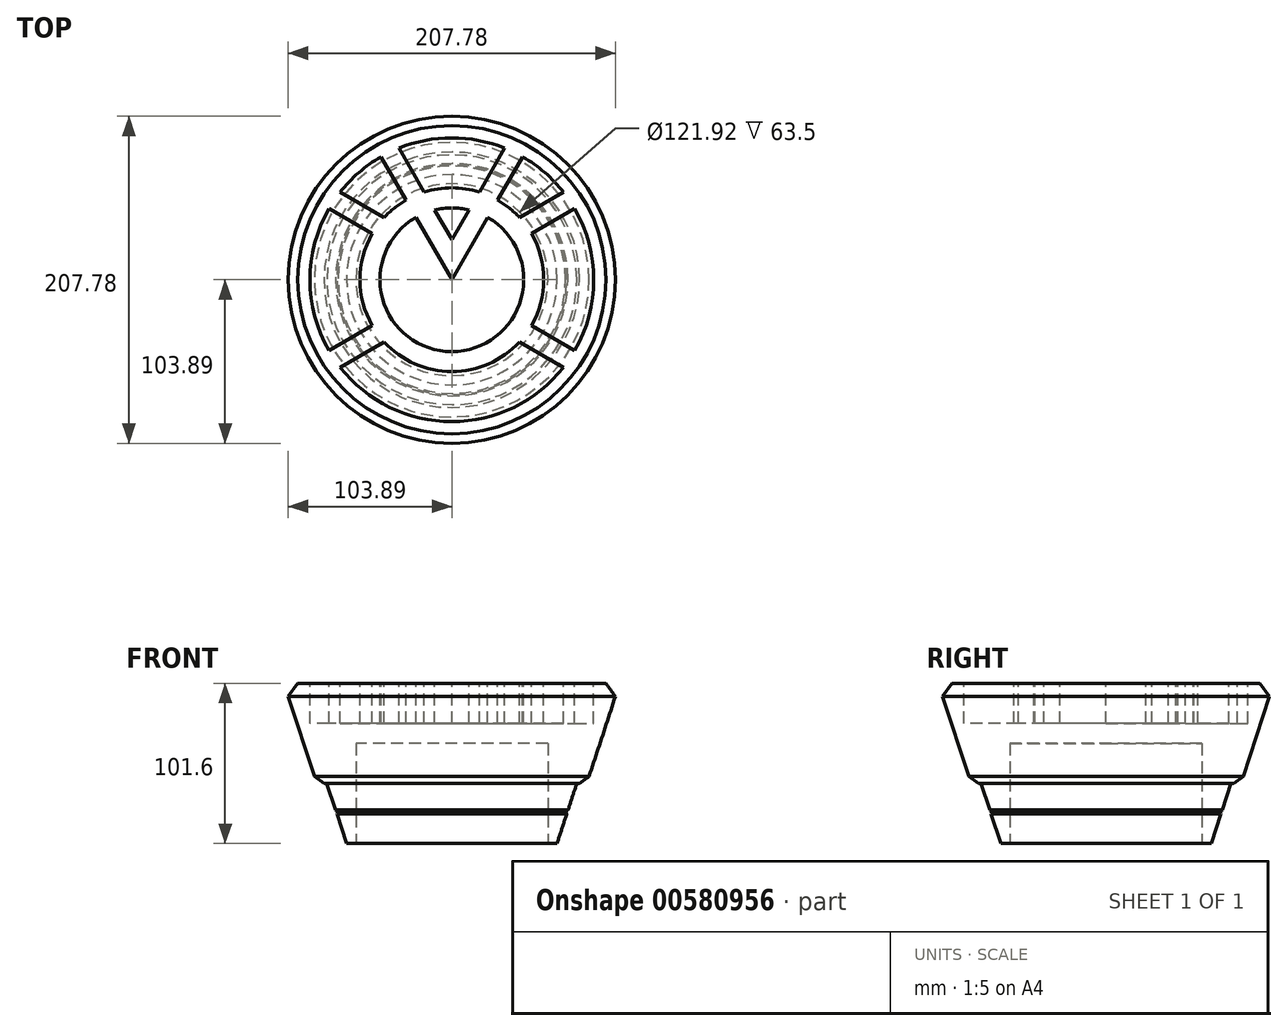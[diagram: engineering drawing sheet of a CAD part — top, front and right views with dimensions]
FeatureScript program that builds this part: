
annotation { "Feature Type Name" : "Feature", "Feature Type Description" : "" }
export const myFeature = defineFeature(function(context is Context, id is Id, definition is map)
    precondition{}
    {
        {
            var Q0;
            Q0=qCreatedBy(makeId("Top.planeOp"),FACE);
            var sketch = newSketch(context, id + "F0", { "sketchPlane" : qUnion([Q0])});
            skCircle(sketch, "E0", {"center": v(0, 0) * mm, "radius": 66.85 * mm});
            skSolve(sketch);
        }
        {
            var Q0;
            Q0=qCreatedBy(makeId("Top.planeOp"),FACE);
            cPlane(context, id + "F1", {"entities" : qUnion([Q0]), "cplaneType" : CPlaneType.OFFSET, "offset" : 101.6 * mm, "width" : 152.4 * mm, "height" : 152.4 * mm});
        }
        {
            var Q0;
            Q0=qCreatedBy(id+"F1.planeOp",FACE);
            var sketch = newSketch(context, id + "F2", { "sketchPlane" : qUnion([Q0])});
            skCircle(sketch, "E1", {"center": v(0, 0) * mm, "radius": 100.28 * mm});
            skSolve(sketch);
        }
        {
            var Q0;
            Q0=makeQuery(id+"F2.imprint","IMPRINT",FACE,{"disambiguationData":[TD([[makeQuery(id+"F2.imprint","IMPRINT",EDGE,{"derivedFrom":sQuery(id+"F2.wireOp",EDGE,"E1")}),1.0]])]});
            var Q1;
            Q1=makeQuery(id+"F0.imprint","IMPRINT",FACE,{"disambiguationData":[TD([[makeQuery(id+"F0.imprint","IMPRINT",EDGE,{"derivedFrom":sQuery(id+"F0.wireOp",EDGE,"E0")}),1.0]])]});
            var Q2;
            Q2=sQuery(id+"F2.wireOp",EDGE,"Eyu8YDiN-lEGU-Wuxt-0ncA-RZLAWeJK4OgB");
            var Q3;
            Q3=sQuery(id+"F0.wireOp",EDGE,"fgfE4CqQ-t5n6-ucAx-yhIW-5wF2yx0Jya2k");
            loft(context, id + "F3", {"sheetProfilesArray" : [{ "sheetProfileEntities" : qUnion([Q0]) }, { "sheetProfileEntities" : qUnion([Q1]) }], "wireProfilesArray" : [{ "wireProfileEntities" : qUnion([Q2]) }, { "wireProfileEntities" : qUnion([Q3]) }]});
        }
        {
            var Q0;
            Q0=qCreatedBy(makeId("Top.planeOp"),FACE);
            cPlane(context, id + "F4", {"entities" : qUnion([Q0]), "cplaneType" : CPlaneType.OFFSET, "offset" : 38.1 * mm, "width" : 152.4 * mm, "height" : 152.4 * mm});
        }
        {
            var Q0;
            Q0=qCreatedBy(id+"F4.planeOp",FACE);
            var sketch = newSketch(context, id + "F5", { "sketchPlane" : qUnion([Q0])});
            skCircle(sketch, "E2", {"center": v(0, 0) * mm, "radius": 85.73 * mm});
            skSolve(sketch);
        }
        {
            var Q0;
            Q0=qCreatedBy(id+"F1.planeOp",FACE);
            var sketch = newSketch(context, id + "F6", { "sketchPlane" : qUnion([Q0])});
            skCircle(sketch, "E3", {"center": v(0, 0) * mm, "radius": 106.63 * mm});
            skSolve(sketch);
        }
        {
            var Q1;
            Q1=makeQuery(id+"F5.imprint","IMPRINT",FACE,{"disambiguationData":[TD([[makeQuery(id+"F5.imprint","IMPRINT",EDGE,{"derivedFrom":sQuery(id+"F5.wireOp",EDGE,"E2")}),1.0]])]});
            var Q2;
            Q2=makeQuery(id+"F6.imprint","IMPRINT",FACE,{"disambiguationData":[TD([[makeQuery(id+"F6.imprint","IMPRINT",EDGE,{"derivedFrom":sQuery(id+"F6.wireOp",EDGE,"E3")}),1.0]])]});
            loft(context, id + "F7", {"operationType" : NewBodyOperationType.ADD, "sheetProfilesArray" : [{ "sheetProfileEntities" : qUnion([Q1]) }, { "sheetProfileEntities" : qUnion([Q2]) }]});
        }
        {
            var Q0;
            Q0=makeQuery(id+"F7.opLoft","MID_CAP_EDGE",EDGE,{"disambiguationData":[OSD([sQuery(id+"F5.wireOp",EDGE,"E2")])],"capPos":0.0});
            chamfer(context, id + "F8", {"entities" : qUnion([Q0]), "width" : 6.35 * mm, "tangentPropagation" : true});
        }
        {
            var Q0;
            Q0=makeQuery(id+"F7.opLoft","MID_CAP_EDGE",EDGE,{"disambiguationData":[OSD([sQuery(id+"F5.wireOp",EDGE,"E2"),sQuery(id+"F6.wireOp",EDGE,"E3")])],"capPos":1.0});
            chamfer(context, id + "F9", {"entities" : qUnion([Q0]), "width" : 6.35 * mm, "tangentPropagation" : true});
        }
        {
            var Q0;
            Q0=qCreatedBy(makeId("Front.planeOp"),FACE);
            var sketch = newSketch(context, id + "F10", { "sketchPlane" : qUnion([Q0])});
            skLineSegment(sketch, "E4", {"start": v(-79.4, 38.11) * mm, "end": v(-66.85, 0) * mm});
            skLineSegment(sketch, "E5", {"start": v(-73.8, 21.14) * mm, "end": v(-72.2, 20.33) * mm});
            skLineSegment(sketch, "E6", {"start": v(-72.2, 20.33) * mm, "end": v(-73.02, 18.73) * mm});
            skSolve(sketch);
        }
        {
            var Q0;
            Q0=qCreatedBy(makeId("Right.planeOp"),FACE);
            var sketch = newSketch(context, id + "F11", { "sketchPlane" : qUnion([Q0])});
            skLineSegment(sketch, "E7", {"start": v(0, 0) * mm, "end": v(0, 184.2) * mm});
            skSolve(sketch);
        }
        {
            var Q0;
            Q0=qSketchRegion(id+"F10",true);
            var Q1;
            Q1=sQuery(id+"F11.wireOp",EDGE,"E7");
            revolve(context, id + "F12", {"operationType" : NewBodyOperationType.REMOVE, "entities" : qUnion([Q0]), "axis" : qUnion([Q1]), "revolveType" : RevolveType.FULL, "oppositeDirection" : true});
        }
        {
            var Q0;
            Q0=makeQuery(id+"F7.boolean.opBoolean","MERGE",FACE,{"derivedFrom":[makeQuery(id+"F3.opLoft","CAP_FACE",FACE,{"disambiguationData":[OSD([makeQuery(id+"F2.imprint","IMPRINT",FACE,{"disambiguationData":[TD([[makeQuery(id+"F2.imprint","IMPRINT",EDGE,{"derivedFrom":sQuery(id+"F2.wireOp",EDGE,"E1")}),1.0]])]})])],"isStart":true}),makeQuery(id+"F7.opLoft","CAP_FACE",FACE,{"disambiguationData":[OSD([makeQuery(id+"F6.imprint","IMPRINT",FACE,{"disambiguationData":[TD([[makeQuery(id+"F6.imprint","IMPRINT",EDGE,{"derivedFrom":sQuery(id+"F6.wireOp",EDGE,"E3")}),1.0]])]})])],"isStart":true})]});
            var sketch = newSketch(context, id + "F13", { "sketchPlane" : qUnion([Q0])});
            skArc(sketch, "E8.0", {"start": v(-218.55, 20.4) * mm, "mid": v(-209.04, -22.5) * mm, "end": v(-199.53, 20.4) * mm});
            skArc(sketch, "E9.0", {"start": v(-205.32, 22.19) * mm, "mid": v(-209.04, 22.5) * mm, "end": v(-212.77, 22.19) * mm});
            skLineSegment(sketch, "E10.0", {"start": v(-212.77, 22.19) * mm, "end": v(-209.04, 14.2) * mm});
            skLineSegment(sketch, "E11.0", {"start": v(-205.32, 22.19) * mm, "end": v(-209.04, 14.2) * mm});
            skLineSegment(sketch, "E12.0", {"start": v(-209.04, 0) * mm, "end": v(-218.55, 20.4) * mm});
            skLineSegment(sketch, "E13.0", {"start": v(-209.04, 0) * mm, "end": v(-199.53, 20.4) * mm});
            skArc(sketch, "E14.0", {"start": v(-184.12, 16.7) * mm, "mid": v(-189.52, 22.78) * mm, "end": v(-196.36, 27.19) * mm});
            skLineSegment(sketch, "E14.1", {"start": v(-184.12, 16.7) * mm, "end": v(-130.82, 33.86) * mm});
            skArc(sketch, "E14.2", {"start": v(-130.82, 33.86) * mm, "mid": v(-147.94, 59.43) * mm, "end": v(-173.02, 77.25) * mm});
            skLineSegment(sketch, "E14.3", {"start": v(-196.36, 27.19) * mm, "end": v(-173.02, 77.25) * mm});
            skLineSegment(sketch, "E14.4", {"start": v(-178.55, 79.6) * mm, "end": v(-202.06, 29.18) * mm});
            skArc(sketch, "E14.5", {"start": v(-178.55, 79.6) * mm, "mid": v(-209.04, 85.24) * mm, "end": v(-239.54, 79.6) * mm});
            skLineSegment(sketch, "E14.6", {"start": v(-239.54, 79.6) * mm, "end": v(-216.03, 29.18) * mm});
            skArc(sketch, "E14.7", {"start": v(-202.06, 29.18) * mm, "mid": v(-209.04, 30) * mm, "end": v(-216.03, 29.18) * mm});
            skArc(sketch, "E14.8", {"start": v(-221.72, 27.19) * mm, "mid": v(-228.56, 22.78) * mm, "end": v(-233.97, 16.7) * mm});
            skLineSegment(sketch, "E14.9", {"start": v(-221.72, 27.19) * mm, "end": v(-245.07, 77.25) * mm});
            skArc(sketch, "E14.10", {"start": v(-245.07, 77.25) * mm, "mid": v(-270.15, 59.43) * mm, "end": v(-287.27, 33.86) * mm});
            skLineSegment(sketch, "E14.11", {"start": v(-233.97, 16.7) * mm, "end": v(-287.27, 33.86) * mm});
            skLineSegment(sketch, "E14.12", {"start": v(-290.18, 26.13) * mm, "end": v(-237.6, 9.2) * mm});
            skArc(sketch, "E14.13", {"start": v(-237.6, 9.2) * mm, "mid": v(-239.04, 0) * mm, "end": v(-237.6, -9.2) * mm});
            skLineSegment(sketch, "E14.14", {"start": v(-290.18, -26.13) * mm, "end": v(-237.6, -9.2) * mm});
            skArc(sketch, "E14.15", {"start": v(-290.18, 26.13) * mm, "mid": v(-294.28, 0) * mm, "end": v(-290.18, -26.13) * mm});
            skLineSegment(sketch, "E14.16", {"start": v(-233.97, -16.7) * mm, "end": v(-287.27, -33.86) * mm});
            skArc(sketch, "E14.17", {"start": v(-287.27, -33.86) * mm, "mid": v(-209.04, -85.24) * mm, "end": v(-130.82, -33.86) * mm});
            skArc(sketch, "E14.18", {"start": v(-233.97, -16.7) * mm, "mid": v(-209.04, -30) * mm, "end": v(-184.12, -16.7) * mm});
            skLineSegment(sketch, "E14.19", {"start": v(-184.12, -16.7) * mm, "end": v(-130.82, -33.86) * mm});
            skLineSegment(sketch, "E14.20", {"start": v(-127.9, -26.13) * mm, "end": v(-180.49, -9.2) * mm});
            skArc(sketch, "E14.21", {"start": v(-180.49, -9.2) * mm, "mid": v(-179.04, 0) * mm, "end": v(-180.49, 9.2) * mm});
            skLineSegment(sketch, "E14.22", {"start": v(-127.9, 26.13) * mm, "end": v(-180.49, 9.2) * mm});
            skArc(sketch, "E14.23", {"start": v(-127.9, -26.13) * mm, "mid": v(-123.8, 0) * mm, "end": v(-127.9, 26.13) * mm});
            skCircle(sketch, "E15.0", {"center": v(-209.04, 0) * mm, "radius": 95.24 * mm});
            skCircle(sketch, "E16", {"center": v(0, 0) * mm, "radius": 100.28 * mm});
            skCircle(sketch, "E17.0", {"center": v(0, 0) * mm, "radius": 90.12 * mm});
            skCircle(sketch, "E18.0", {"center": v(0, 0) * mm, "radius": 58.37 * mm});
            skCircle(sketch, "E19.0", {"center": v(0, 0) * mm, "radius": 45.67 * mm});
            skLineSegment(sketch, "E20", {"start": v(0, 0) * mm, "end": v(-50.14, 86.84) * mm});
            skLineSegment(sketch, "E21", {"start": v(0, 0) * mm, "end": v(50.14, 86.84) * mm});
            skLineSegment(sketch, "E22.0", {"start": v(0, 25.4) * mm, "end": v(-38.74, 92.5) * mm});
            skLineSegment(sketch, "E23.0", {"start": v(0, 25.4) * mm, "end": v(38.74, 92.5) * mm});
            skLineSegment(sketch, "E24", {"start": v(0, 0) * mm, "end": v(-86.84, 50.14) * mm});
            skLineSegment(sketch, "E25.0", {"start": v(-42.99, 39.48) * mm, "end": v(-79.8, 60.73) * mm});
            skLineSegment(sketch, "E26", {"start": v(0, 0) * mm, "end": v(-86.3, 0) * mm});
            skLineSegment(sketch, "E27", {"start": v(0, 25.4) * mm, "end": v(0, 0) * mm});
            skLineSegment(sketch, "E28.MirrorCS", {"start": v(42.99, 39.48) * mm, "end": v(79.8, 60.73) * mm});
            skLineSegment(sketch, "E29.MirrorCS", {"start": v(0, 0) * mm, "end": v(86.84, 50.14) * mm});
            skLineSegment(sketch, "E30.MirrorCS", {"start": v(0, 0) * mm, "end": v(-86.84, -50.14) * mm});
            skLineSegment(sketch, "E31.MirrorCS", {"start": v(-42.99, -39.48) * mm, "end": v(-79.8, -60.73) * mm});
            skLineSegment(sketch, "E32.MirrorCS", {"start": v(42.99, -39.48) * mm, "end": v(79.8, -60.73) * mm});
            skLineSegment(sketch, "E33.MirrorCS", {"start": v(0, 0) * mm, "end": v(86.84, -50.14) * mm});
            skSolve(sketch);
        }
        {
            var Q0;
            {var subQ4=sQuery(id+"F13.wireOp",EDGE,"E24");var subQ6=sQuery(id+"F13.wireOp",EDGE,"E17.0");var subQ7=makeQuery(id+"F13.imprint","INTERSECT",VERTEX,{"derivedFrom":[subQ6,subQ4]});Q0=makeQuery(id+"F13.imprint","IMPRINT",FACE,{"disambiguationData":[TD([[makeQuery(id+"F13.imprint","IMPRINT",EDGE,{"disambiguationData":[TD([[subQ7,-1.0]])],"derivedFrom":subQ6}),1.0]])]});}
            var Q1;
            {var subQ0=sQuery(id+"F13.wireOp",EDGE,"E31.MirrorCS");var subQ1=sQuery(id+"F13.wireOp",EDGE,"E17.0");var subQ2=makeQuery(id+"F13.imprint","INTERSECT",VERTEX,{"derivedFrom":[subQ1,subQ0]});Q1=makeQuery(id+"F13.imprint","IMPRINT",FACE,{"disambiguationData":[TD([[makeQuery(id+"F13.imprint","IMPRINT",EDGE,{"disambiguationData":[TD([[subQ2,-1.0]])],"derivedFrom":subQ1}),1.0]])]});}
            var Q2;
            {var subQ0=sQuery(id+"F13.wireOp",EDGE,"E29.MirrorCS");var subQ1=sQuery(id+"F13.wireOp",EDGE,"E17.0");var subQ2=makeQuery(id+"F13.imprint","INTERSECT",VERTEX,{"derivedFrom":[subQ1,subQ0]});Q2=makeQuery(id+"F13.imprint","IMPRINT",FACE,{"disambiguationData":[TD([[makeQuery(id+"F13.imprint","IMPRINT",EDGE,{"disambiguationData":[TD([[subQ2,1.0]])],"derivedFrom":subQ1}),1.0]])]});}
            var Q3;
            {var subQ0=sQuery(id+"F13.wireOp",EDGE,"E28.MirrorCS");var subQ1=sQuery(id+"F13.wireOp",EDGE,"E17.0");var subQ2=makeQuery(id+"F13.imprint","INTERSECT",VERTEX,{"derivedFrom":[subQ1,subQ0]});Q3=makeQuery(id+"F13.imprint","IMPRINT",FACE,{"disambiguationData":[TD([[makeQuery(id+"F13.imprint","IMPRINT",EDGE,{"disambiguationData":[TD([[subQ2,-1.0]])],"derivedFrom":subQ1}),1.0]])]});}
            var Q4;
            {var subQ0=sQuery(id+"F13.wireOp",EDGE,"E23.0");var subQ1=sQuery(id+"F13.wireOp",EDGE,"E17.0");var subQ2=makeQuery(id+"F13.imprint","INTERSECT",VERTEX,{"derivedFrom":[subQ1,subQ0]});Q4=makeQuery(id+"F13.imprint","IMPRINT",FACE,{"disambiguationData":[TD([[makeQuery(id+"F13.imprint","IMPRINT",EDGE,{"disambiguationData":[TD([[subQ2,-1.0]])],"derivedFrom":subQ1}),1.0]])]});}
            var Q5;
            {var subQ0=sQuery(id+"F13.wireOp",EDGE,"E20");var subQ1=sQuery(id+"F13.wireOp",EDGE,"E17.0");var subQ2=makeQuery(id+"F13.imprint","INTERSECT",VERTEX,{"derivedFrom":[subQ1,subQ0]});Q5=makeQuery(id+"F13.imprint","IMPRINT",FACE,{"disambiguationData":[TD([[makeQuery(id+"F13.imprint","IMPRINT",EDGE,{"disambiguationData":[TD([[subQ2,-1.0]])],"derivedFrom":subQ1}),1.0]])]});}
            var Q6;
            {var subQ0=sQuery(id+"F13.wireOp",EDGE,"E30.MirrorCS");var subQ1=sQuery(id+"F13.wireOp",EDGE,"E19.0");var subQ2=makeQuery(id+"F13.imprint","INTERSECT",VERTEX,{"derivedFrom":[subQ1,subQ0]});Q6=makeQuery(id+"F13.imprint","IMPRINT",FACE,{"disambiguationData":[TD([[makeQuery(id+"F13.imprint","IMPRINT",EDGE,{"disambiguationData":[TD([[subQ2,-1.0]])],"derivedFrom":subQ1}),1.0]])]});}
            var Q7;
            {var subQ0=sQuery(id+"F13.wireOp",EDGE,"E26");var subQ1=sQuery(id+"F13.wireOp",EDGE,"E19.0");var subQ2=makeQuery(id+"F13.imprint","INTERSECT",VERTEX,{"derivedFrom":[subQ1,subQ0]});Q7=makeQuery(id+"F13.imprint","IMPRINT",FACE,{"disambiguationData":[TD([[makeQuery(id+"F13.imprint","IMPRINT",EDGE,{"disambiguationData":[TD([[subQ2,-1.0]])],"derivedFrom":subQ1}),1.0]])]});}
            var Q8;
            {var subQ0=sQuery(id+"F13.wireOp",EDGE,"E24");var subQ1=sQuery(id+"F13.wireOp",EDGE,"E19.0");var subQ2=makeQuery(id+"F13.imprint","INTERSECT",VERTEX,{"derivedFrom":[subQ1,subQ0]});Q8=makeQuery(id+"F13.imprint","IMPRINT",FACE,{"disambiguationData":[TD([[makeQuery(id+"F13.imprint","IMPRINT",EDGE,{"disambiguationData":[TD([[subQ2,-1.0]])],"derivedFrom":subQ1}),1.0]])]});}
            var Q9;
            {var subQ0=sQuery(id+"F13.wireOp",EDGE,"E29.MirrorCS");var subQ1=sQuery(id+"F13.wireOp",EDGE,"E19.0");var subQ2=makeQuery(id+"F13.imprint","INTERSECT",VERTEX,{"derivedFrom":[subQ1,subQ0]});Q9=makeQuery(id+"F13.imprint","IMPRINT",FACE,{"disambiguationData":[TD([[makeQuery(id+"F13.imprint","IMPRINT",EDGE,{"disambiguationData":[TD([[subQ2,1.0]])],"derivedFrom":subQ1}),1.0]])]});}
            var Q10;
            {var subQ0=sQuery(id+"F13.wireOp",EDGE,"E21");var subQ1=sQuery(id+"F13.wireOp",EDGE,"E19.0");var subQ2=makeQuery(id+"F13.imprint","INTERSECT",VERTEX,{"derivedFrom":[subQ1,subQ0]});Q10=makeQuery(id+"F13.imprint","IMPRINT",FACE,{"disambiguationData":[TD([[makeQuery(id+"F13.imprint","IMPRINT",EDGE,{"disambiguationData":[TD([[subQ2,1.0]])],"derivedFrom":subQ1}),1.0]])]});}
            var Q11;
            {var subQ0=sQuery(id+"F13.wireOp",EDGE,"E20");var subQ1=sQuery(id+"F13.wireOp",EDGE,"E19.0");var subQ2=makeQuery(id+"F13.imprint","INTERSECT",VERTEX,{"derivedFrom":[subQ1,subQ0]});Q11=makeQuery(id+"F13.imprint","IMPRINT",FACE,{"disambiguationData":[TD([[makeQuery(id+"F13.imprint","IMPRINT",EDGE,{"disambiguationData":[TD([[subQ2,-1.0]])],"derivedFrom":subQ1}),1.0]])]});}
            var Q12;
            {var subQ0=sQuery(id+"F13.wireOp",EDGE,"E23.0");var subQ1=sQuery(id+"F13.wireOp",EDGE,"E19.0");var subQ2=makeQuery(id+"F13.imprint","INTERSECT",VERTEX,{"derivedFrom":[subQ1,subQ0]});Q12=makeQuery(id+"F13.imprint","IMPRINT",FACE,{"disambiguationData":[TD([[makeQuery(id+"F13.imprint","IMPRINT",EDGE,{"disambiguationData":[TD([[subQ2,-1.0]])],"derivedFrom":subQ1}),1.0]])]});}
            extrude(context, id + "F14", {"entities" : qUnion([Q0, Q1, Q2, Q3, Q4, Q5, Q6, Q7, Q8, Q9, Q10, Q11, Q12]), "operationType" : NewBodyOperationType.REMOVE, "oppositeDirection" : true, "depth" : 25.4 * mm, "offsetDistance" : 25.4 * mm});
        }
        {
            var Q0;
            Q0=qCreatedBy(makeId("Top.planeOp"),FACE);
            var sketch = newSketch(context, id + "F15", { "sketchPlane" : qUnion([Q0])});
            skCircle(sketch, "E34", {"center": v(0, 0) * mm, "radius": 60.96 * mm});
            skSolve(sketch);
        }
        {
            var Q0;
            Q0=makeQuery(id+"F15.imprint","IMPRINT",FACE,{"disambiguationData":[TD([[makeQuery(id+"F15.imprint","IMPRINT",EDGE,{"derivedFrom":sQuery(id+"F15.wireOp",EDGE,"E34")}),1.0]])]});
            extrude(context, id + "F16", {"entities" : qUnion([Q0]), "operationType" : NewBodyOperationType.REMOVE, "depth" : 63.5 * mm, "offsetDistance" : 25.4 * mm});
        }
    });
